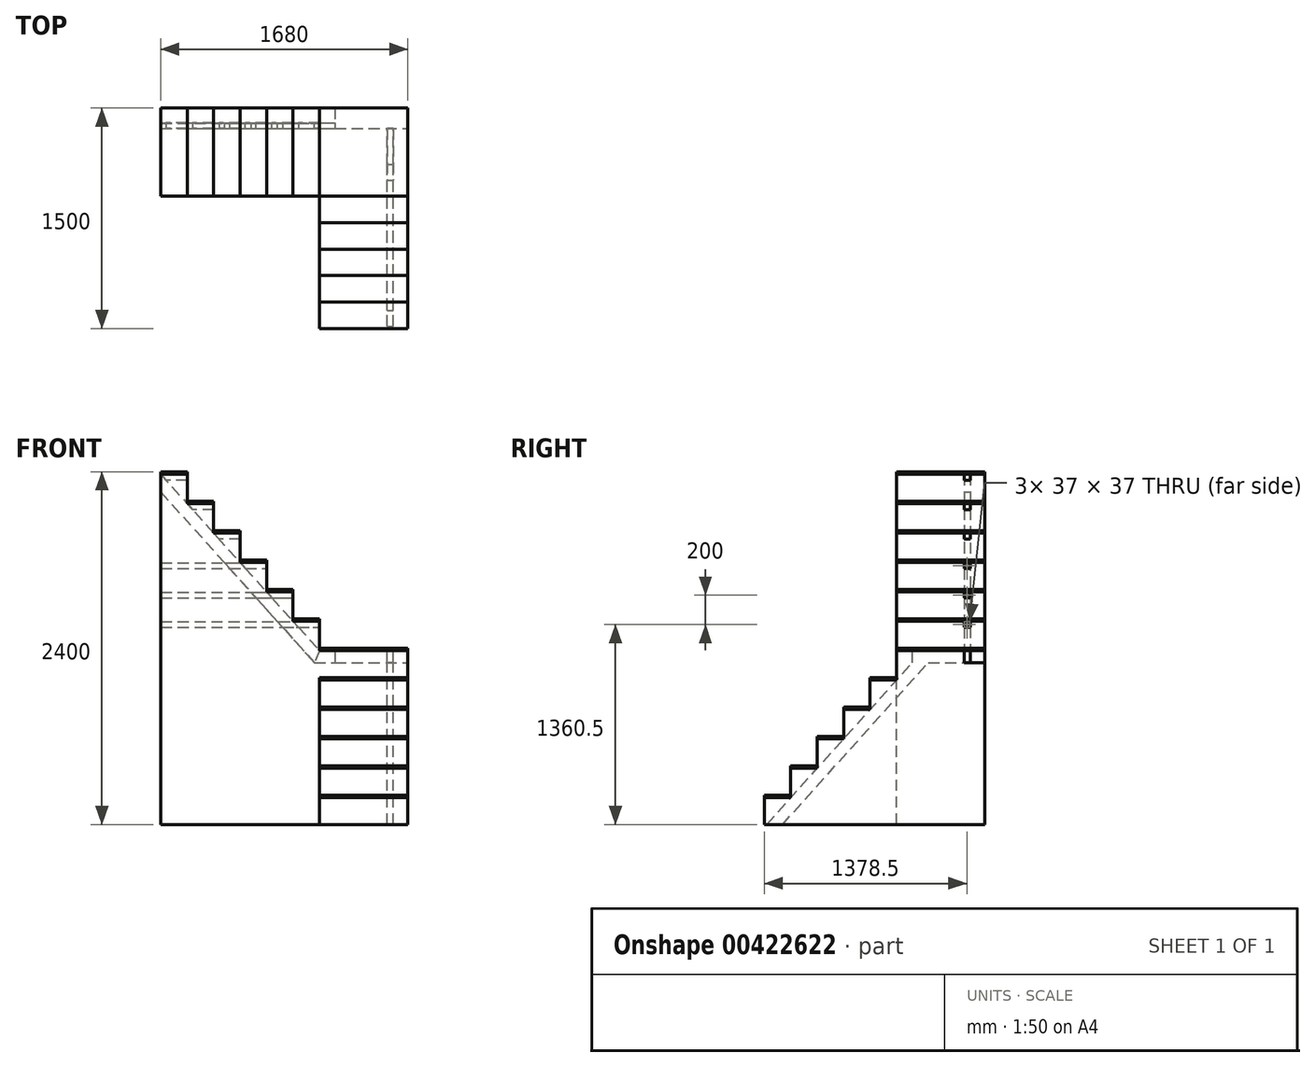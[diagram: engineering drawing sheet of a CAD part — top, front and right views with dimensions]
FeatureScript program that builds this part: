
annotation { "Feature Type Name" : "Feature", "Feature Type Description" : "" }
export const myFeature = defineFeature(function(context is Context, id is Id, definition is map)
    precondition{}
    {
        {
            var Q0;
            Q0=qCreatedBy(makeId("Front.planeOp"),FACE);
            var sketch = newSketch(context, id + "F0", { "sketchPlane" : qUnion([Q0])});
            skLineSegment(sketch, "E0.bottom", {"start": v(0, 0) * mm, "end": v(-600, 0) * mm});
            skLineSegment(sketch, "E0.top", {"start": v(0, 1200) * mm, "end": v(-600, 1200) * mm});
            skLineSegment(sketch, "E0.left", {"start": v(0, 0) * mm, "end": v(0, 1200) * mm});
            skLineSegment(sketch, "E0.right", {"start": v(-600, 0) * mm, "end": v(-600, 1200) * mm, "construction": true});
            skLineSegment(sketch, "E1", {"start": v(-600, 1200) * mm, "end": v(-600, 1400) * mm});
            skLineSegment(sketch, "E2", {"start": v(-600, 1400) * mm, "end": v(-780, 1400) * mm});
            skLineSegment(sketch, "E3", {"start": v(-780, 1400) * mm, "end": v(-780, 1600) * mm});
            skLineSegment(sketch, "E4", {"start": v(-780, 1600) * mm, "end": v(-960, 1600) * mm});
            skLineSegment(sketch, "E5", {"start": v(-960, 1600) * mm, "end": v(-960, 1800) * mm});
            skLineSegment(sketch, "E6", {"start": v(-960, 1800) * mm, "end": v(-1140, 1800) * mm});
            skLineSegment(sketch, "E7", {"start": v(-1140, 1800) * mm, "end": v(-1140, 2000) * mm});
            skLineSegment(sketch, "E8", {"start": v(-1140, 2000) * mm, "end": v(-1320, 2000) * mm});
            skLineSegment(sketch, "E9", {"start": v(-1320, 2000) * mm, "end": v(-1320, 2200) * mm});
            skLineSegment(sketch, "E10", {"start": v(-1320, 2200) * mm, "end": v(-1500, 2200) * mm});
            skLineSegment(sketch, "E11", {"start": v(-1500, 2200) * mm, "end": v(-1500, 2400) * mm});
            skLineSegment(sketch, "E12", {"start": v(-1500, 2400) * mm, "end": v(-1680, 2400) * mm});
            skLineSegment(sketch, "E13", {"start": v(-1680, 2400) * mm, "end": v(-1680, 0) * mm});
            skLineSegment(sketch, "E14", {"start": v(-1680, 0) * mm, "end": v(-600, 0) * mm});
            skLineSegment(sketch, "E15", {"start": v(-1680, 2400) * mm, "end": v(-1680, 2600) * mm, "construction": true});
            skLineSegment(sketch, "E16", {"start": v(-1680, 2600) * mm, "end": v(-2502.05, 2600) * mm, "construction": true});
            skLineSegment(sketch, "E17", {"start": v(-1680, 2582) * mm, "end": v(-2575.09, 2582) * mm, "construction": true});
            skLineSegment(sketch, "E18", {"start": v(-1680, 2382) * mm, "end": v(-1730, 2382) * mm, "construction": true});
            skLineSegment(sketch, "E19", {"start": v(-1730, 2382) * mm, "end": v(-1730, 2582) * mm, "construction": true});
            skSolve(sketch);
        }
        {
            var Q0;
            Q0=makeQuery(id+"F0.imprint","IMPRINT",FACE,{"disambiguationData":[TD([[makeQuery(id+"F0.imprint","IMPRINT",EDGE,{"derivedFrom":sQuery(id+"F0.wireOp",EDGE,"E0.bottom")}),-1.0]])]});
            extrude(context, id + "F1", {"entities" : qUnion([Q0]), "depth" : 600 * mm});
        }
        {
            var Q0;
            Q0=makeQuery(id+"F1.opExtrude","SWEPT_FACE",FACE,{"disambiguationData":[OSD([sQuery(id+"F0.wireOp",EDGE,"E0.left")])]});
            var sketch = newSketch(context, id + "F2", { "sketchPlane" : qUnion([Q0])});
            skLineSegment(sketch, "E20", {"start": v(-600, 0) * mm, "end": v(-1500, 0) * mm});
            skLineSegment(sketch, "E21", {"start": v(-1500, 0) * mm, "end": v(-1500, 200) * mm});
            skLineSegment(sketch, "E22", {"start": v(-1500, 200) * mm, "end": v(-1320, 200) * mm});
            skLineSegment(sketch, "E23", {"start": v(-1320, 200) * mm, "end": v(-1320, 400) * mm});
            skLineSegment(sketch, "E24", {"start": v(-1320, 400) * mm, "end": v(-1140, 400) * mm});
            skLineSegment(sketch, "E25", {"start": v(-1140, 400) * mm, "end": v(-1140, 600) * mm});
            skLineSegment(sketch, "E26", {"start": v(-1140, 600) * mm, "end": v(-960, 600) * mm});
            skLineSegment(sketch, "E27", {"start": v(-960, 600) * mm, "end": v(-960, 800) * mm});
            skLineSegment(sketch, "E28", {"start": v(-960, 800) * mm, "end": v(-780, 800) * mm});
            skLineSegment(sketch, "E29", {"start": v(-780, 800) * mm, "end": v(-780, 1000) * mm});
            skLineSegment(sketch, "E30", {"start": v(-780, 1000) * mm, "end": v(-600, 1000) * mm});
            skSolve(sketch);
        }
        {
            var Q0;
            Q0 = qSketchRegion(id + "F2", true);
            var Q1;
            {var subQ0=sQuery(id+"F2.wireOp",EDGE,"E20");Q1=makeQuery(id+"F2.imprint","IMPRINT",FACE,{"disambiguationData":[TD([[makeQuery(id+"F2.imprint","IMPRINT",EDGE,{"derivedFrom":subQ0}),-1.0]])]});}
            extrude(context, id + "F3", {"entities" : qUnion([Q0, Q1]), "operationType" : NewBodyOperationType.ADD, "oppositeDirection" : true, "depth" : 600 * mm});
        }
        {
            var Q0;
            Q0=makeQuery(id+"F1.opExtrude","SWEPT_FACE",FACE,{"disambiguationData":[OSD([sQuery(id+"F0.wireOp",EDGE,"E12")])]});
            var Q1;
            Q1=makeQuery(id+"F1.opExtrude","SWEPT_FACE",FACE,{"disambiguationData":[OSD([sQuery(id+"F0.wireOp",EDGE,"E10")])]});
            var Q2;
            Q2=makeQuery(id+"F1.opExtrude","SWEPT_FACE",FACE,{"disambiguationData":[OSD([sQuery(id+"F0.wireOp",EDGE,"E8")])]});
            var Q3;
            Q3=makeQuery(id+"F1.opExtrude","SWEPT_FACE",FACE,{"disambiguationData":[OSD([sQuery(id+"F0.wireOp",EDGE,"E6")])]});
            var Q4;
            Q4=makeQuery(id+"F1.opExtrude","SWEPT_FACE",FACE,{"disambiguationData":[OSD([sQuery(id+"F0.wireOp",EDGE,"E4")])]});
            var Q5;
            Q5=makeQuery(id+"F1.opExtrude","SWEPT_FACE",FACE,{"disambiguationData":[OSD([sQuery(id+"F0.wireOp",EDGE,"E2")])]});
            var Q6;
            Q6=makeQuery(id+"F1.opExtrude","SWEPT_FACE",FACE,{"disambiguationData":[OSD([sQuery(id+"F0.wireOp",EDGE,"E0.top")])]});
            var Q7;
            Q7=makeQuery(id+"F3.opExtrude","SWEPT_FACE",FACE,{"disambiguationData":[OSD([sQuery(id+"F2.wireOp",EDGE,"E30")])]});
            var Q8;
            Q8=makeQuery(id+"F3.opExtrude","SWEPT_FACE",FACE,{"disambiguationData":[OSD([sQuery(id+"F2.wireOp",EDGE,"E28")])]});
            var Q9;
            Q9=makeQuery(id+"F3.opExtrude","SWEPT_FACE",FACE,{"disambiguationData":[OSD([sQuery(id+"F2.wireOp",EDGE,"E26")])]});
            var Q10;
            Q10=makeQuery(id+"F3.opExtrude","SWEPT_FACE",FACE,{"disambiguationData":[OSD([sQuery(id+"F2.wireOp",EDGE,"E24")])]});
            var Q11;
            Q11=makeQuery(id+"F3.opExtrude","SWEPT_FACE",FACE,{"disambiguationData":[OSD([sQuery(id+"F2.wireOp",EDGE,"E22")])]});
            extrude(context, id + "F4", {"entities" : qUnion([Q0, Q1, Q2, Q3, Q4, Q5, Q6, Q7, Q8, Q9, Q10, Q11]), "oppositeDirection" : true, "depth" : 18 * mm});
        }
        {
            var Q0;
            Q0=qCreatedBy(makeId("Front.planeOp"),FACE);
            cPlane(context, id + "F5", {"entities" : qUnion([Q0]), "cplaneType" : CPlaneType.OFFSET, "offset" : 100 * mm, "width" : 150 * mm, "height" : 150 * mm});
        }
        {
            var Q0;
            Q0=qCreatedBy(id+"F5.planeOp",FACE);
            var sketch = newSketch(context, id + "F6", { "sketchPlane" : qUnion([Q0])});
            skLineSegment(sketch, "E31", {"start": v(-1680, 2382) * mm, "end": v(-600, 1182) * mm});
            skLineSegment(sketch, "E32", {"start": v(-1680, 2382) * mm, "end": v(-1680, 2262.41) * mm});
            skLineSegment(sketch, "E33", {"start": v(-1680, 2262.41) * mm, "end": v(-635.63, 1102) * mm});
            skLineSegment(sketch, "E34", {"start": v(-635.63, 1102) * mm, "end": v(-600, 1182) * mm});
            skLineSegment(sketch, "E35", {"start": v(-600, 1182) * mm, "end": v(-535.87, 1182) * mm, "construction": true});
            skSolve(sketch);
        }
        {
            var Q0;
            Q0 = qSketchRegion(id + "F6", true);
            extrude(context, id + "F7", {"entities" : qUnion([Q0]), "depth" : 40 * mm});
        }
        {
            var Q0;
            Q0=qCreatedBy(id+"F5.planeOp",FACE);
            var sketch = newSketch(context, id + "F8", { "sketchPlane" : qUnion([Q0])});
            skLineSegment(sketch, "E36.bottom", {"start": v(-600, 1182) * mm, "end": v(0, 1182) * mm});
            skLineSegment(sketch, "E36.top", {"start": v(-635.63, 1102) * mm, "end": v(0, 1102) * mm});
            skLineSegment(sketch, "E36.right", {"start": v(0, 1182) * mm, "end": v(0, 1102) * mm});
            skLineSegment(sketch, "E37", {"start": v(-600, 1182) * mm, "end": v(-635.63, 1102) * mm});
            skSolve(sketch);
        }
        {
            var Q0;
            Q0 = qSketchRegion(id + "F8", true);
            extrude(context, id + "F9", {"entities" : qUnion([Q0]), "depth" : 40 * mm});
        }
        {
            var Q0;
            Q0=makeQuery(id+"F7.opExtrude","CAP_FACE",FACE,{"disambiguationData":[OSD([sQuery(id+"F6.wireOp",EDGE,"E31"),sQuery(id+"F6.wireOp",EDGE,"E32"),sQuery(id+"F6.wireOp",EDGE,"E33"),sQuery(id+"F6.wireOp",EDGE,"E34")])],"isStart":false});
            var sketch = newSketch(context, id + "F10", { "sketchPlane" : qUnion([Q0])});
            skLineSegment(sketch, "E38", {"start": v(-1680, 2382) * mm, "end": v(-1500, 2382) * mm});
            skLineSegment(sketch, "E39", {"start": v(-1500, 2382) * mm, "end": v(-1500, 2342) * mm});
            skLineSegment(sketch, "E40", {"start": v(-1500, 2342) * mm, "end": v(-1644, 2342) * mm});
            skLineSegment(sketch, "E41", {"start": v(-1644, 2342) * mm, "end": v(-1680, 2382) * mm});
            skLineSegment(sketch, "E42.1.0.0", {"start": v(-1500, 2182) * mm, "end": v(-1320, 2182) * mm});
            skLineSegment(sketch, "E42.1.0.1", {"start": v(-1320, 2142) * mm, "end": v(-1464, 2142) * mm});
            skLineSegment(sketch, "E42.1.0.2", {"start": v(-1464, 2142) * mm, "end": v(-1500, 2182) * mm});
            skLineSegment(sketch, "E42.1.0.3", {"start": v(-1320, 2182) * mm, "end": v(-1320, 2142) * mm});
            skLineSegment(sketch, "E42.2.0.0", {"start": v(-1320, 1982) * mm, "end": v(-1140, 1982) * mm});
            skLineSegment(sketch, "E42.2.0.1", {"start": v(-1140, 1942) * mm, "end": v(-1284, 1942) * mm});
            skLineSegment(sketch, "E42.2.0.2", {"start": v(-1284, 1942) * mm, "end": v(-1320, 1982) * mm});
            skLineSegment(sketch, "E42.2.0.3", {"start": v(-1140, 1982) * mm, "end": v(-1140, 1942) * mm});
            skLineSegment(sketch, "E42.3.0.0", {"start": v(-1140, 1782) * mm, "end": v(-960, 1782) * mm});
            skLineSegment(sketch, "E42.3.0.1", {"start": v(-960, 1742) * mm, "end": v(-1104, 1742) * mm});
            skLineSegment(sketch, "E42.3.0.2", {"start": v(-1104, 1742) * mm, "end": v(-1140, 1782) * mm});
            skLineSegment(sketch, "E42.3.0.3", {"start": v(-960, 1782) * mm, "end": v(-960, 1742) * mm});
            skLineSegment(sketch, "E42.4.0.0", {"start": v(-960, 1582) * mm, "end": v(-780, 1582) * mm});
            skLineSegment(sketch, "E42.4.0.1", {"start": v(-780, 1542) * mm, "end": v(-924, 1542) * mm});
            skLineSegment(sketch, "E42.4.0.2", {"start": v(-924, 1542) * mm, "end": v(-960, 1582) * mm});
            skLineSegment(sketch, "E42.4.0.3", {"start": v(-780, 1582) * mm, "end": v(-780, 1542) * mm});
            skLineSegment(sketch, "E42.5.0.0", {"start": v(-780, 1382) * mm, "end": v(-600, 1382) * mm});
            skLineSegment(sketch, "E42.5.0.1", {"start": v(-600, 1342) * mm, "end": v(-744, 1342) * mm});
            skLineSegment(sketch, "E42.5.0.2", {"start": v(-744, 1342) * mm, "end": v(-780, 1382) * mm});
            skLineSegment(sketch, "E42.5.0.3", {"start": v(-600, 1382) * mm, "end": v(-600, 1342) * mm});
            skLineSegment(sketch, "E42.direction1", {"start": v(-1644, 2342) * mm, "end": v(-1464, 2142) * mm, "construction": true});
            skSolve(sketch);
        }
        {
            var Q0;
            Q0 = qSketchRegion(id + "F10", true);
            extrude(context, id + "F11", {"entities" : qUnion([Q0]), "oppositeDirection" : true, "depth" : 40 * mm});
        }
        {
            var Q0;
            Q0=makeQuery(id+"F11.opExtrude","SWEPT_FACE",FACE,{"disambiguationData":[OSD([sQuery(id+"F10.wireOp",EDGE,"E42.5.0.3")])]});
            var sketch = newSketch(context, id + "F12", { "sketchPlane" : qUnion([Q0])});
            skLineSegment(sketch, "E43.bottom", {"start": v(-140, 1342) * mm, "end": v(-103, 1342) * mm});
            skLineSegment(sketch, "E43.top", {"start": v(-140, 1379) * mm, "end": v(-103, 1379) * mm});
            skLineSegment(sketch, "E43.left", {"start": v(-140, 1342) * mm, "end": v(-140, 1379) * mm});
            skLineSegment(sketch, "E43.right", {"start": v(-103, 1342) * mm, "end": v(-103, 1379) * mm});
            skLineSegment(sketch, "E44.bottom", {"start": v(-140, 1542) * mm, "end": v(-103, 1542) * mm});
            skLineSegment(sketch, "E44.top", {"start": v(-140, 1579) * mm, "end": v(-103, 1579) * mm});
            skLineSegment(sketch, "E44.left", {"start": v(-140, 1542) * mm, "end": v(-140, 1579) * mm});
            skLineSegment(sketch, "E44.right", {"start": v(-103, 1542) * mm, "end": v(-103, 1579) * mm});
            skLineSegment(sketch, "E45.bottom", {"start": v(-140, 1742) * mm, "end": v(-103, 1742) * mm});
            skLineSegment(sketch, "E45.top", {"start": v(-140, 1779) * mm, "end": v(-103, 1779) * mm});
            skLineSegment(sketch, "E45.left", {"start": v(-140, 1742) * mm, "end": v(-140, 1779) * mm});
            skLineSegment(sketch, "E45.right", {"start": v(-103, 1742) * mm, "end": v(-103, 1779) * mm});
            skSolve(sketch);
        }
        {
            var Q0;
            Q0=makeQuery(id+"F12.imprint","IMPRINT",FACE,{"disambiguationData":[TD([[makeQuery(id+"F12.imprint","IMPRINT",EDGE,{"derivedFrom":sQuery(id+"F12.wireOp",EDGE,"E43.bottom")}),-1.0]])]});
            var Q1;
            Q1=makeQuery(id+"F12.imprint","IMPRINT",FACE,{"disambiguationData":[TD([[makeQuery(id+"F12.imprint","IMPRINT",EDGE,{"derivedFrom":sQuery(id+"F12.wireOp",EDGE,"E44.bottom")}),1.0]])]});
            var Q2;
            Q2=makeQuery(id+"F12.imprint","IMPRINT",FACE,{"disambiguationData":[TD([[makeQuery(id+"F12.imprint","IMPRINT",EDGE,{"derivedFrom":sQuery(id+"F12.wireOp",EDGE,"E45.bottom")}),1.0]])]});
            extrude(context, id + "F13", {"entities" : qUnion([Q0, Q1, Q2]), "operationType" : NewBodyOperationType.REMOVE, "endBound" : BoundingType.THROUGH_ALL, "oppositeDirection" : true, "depth" : 25 * mm});
        }
        {
            var Q0;
            Q0=qCreatedBy(makeId("Right.planeOp"),FACE);
            cPlane(context, id + "F14", {"entities" : qUnion([Q0]), "cplaneType" : CPlaneType.OFFSET, "offset" : 100 * mm, "oppositeDirection" : true, "width" : 150 * mm, "height" : 150 * mm});
        }
        {
            var Q0;
            Q0=qCreatedBy(id+"F14.planeOp",FACE);
            var sketch = newSketch(context, id + "F15", { "sketchPlane" : qUnion([Q0])});
            skLineSegment(sketch, "E46", {"start": v(-1483.8, 0) * mm, "end": v(-420, 1182) * mm});
            skLineSegment(sketch, "E47", {"start": v(-1483.8, 0) * mm, "end": v(-1376.17, 0) * mm});
            skLineSegment(sketch, "E48", {"start": v(-1376.17, 0) * mm, "end": v(-384.37, 1102) * mm});
            skLineSegment(sketch, "E49", {"start": v(-420, 1182) * mm, "end": v(-384.37, 1102) * mm});
            skLineSegment(sketch, "E50", {"start": v(-384.37, 1102) * mm, "end": v(-384.37, 1182) * mm, "construction": true});
            skLineSegment(sketch, "E51", {"start": v(-420, 1182) * mm, "end": v(0, 1182) * mm});
            skLineSegment(sketch, "E52", {"start": v(-384.37, 1102) * mm, "end": v(0, 1102) * mm});
            skLineSegment(sketch, "E53", {"start": v(0, 1102) * mm, "end": v(0, 1182) * mm});
            skLineSegment(sketch, "E54", {"start": v(-492, 1102) * mm, "end": v(-492, 1182) * mm});
            skLineSegment(sketch, "E55", {"start": v(-420, 1182) * mm, "end": v(-492, 1182) * mm});
            skSolve(sketch);
        }
        {
            var Q0;
            Q0 = qSketchRegion(id + "F15", true);
            extrude(context, id + "F16", {"entities" : qUnion([Q0]), "oppositeDirection" : true, "depth" : 40 * mm});
        }
        {
            var Q0;
            Q0=makeQuery(id+"F9.opExtrude","CAP_FACE",FACE,{"disambiguationData":[OSD([sQuery(id+"F8.wireOp",EDGE,"E36.bottom"),sQuery(id+"F8.wireOp",EDGE,"E36.top"),sQuery(id+"F8.wireOp",EDGE,"E36.right"),sQuery(id+"F8.wireOp",EDGE,"E37")])],"isStart":false});
            var sketch = newSketch(context, id + "F17", { "sketchPlane" : qUnion([Q0])});
            skLineSegment(sketch, "E56.bottom", {"start": v(-495.76, 1182) * mm, "end": v(0, 1182) * mm});
            skLineSegment(sketch, "E56.top", {"start": v(-495.76, 1102) * mm, "end": v(0, 1102) * mm});
            skLineSegment(sketch, "E56.left", {"start": v(-495.76, 1182) * mm, "end": v(-495.76, 1102) * mm});
            skLineSegment(sketch, "E56.right", {"start": v(0, 1182) * mm, "end": v(0, 1102) * mm});
            skSolve(sketch);
        }
        {
            var Q0;
            Q0 = qSketchRegion(id + "F17", true);
            extrude(context, id + "F18", {"entities" : qUnion([Q0]), "operationType" : NewBodyOperationType.REMOVE, "endBound" : BoundingType.THROUGH_ALL, "oppositeDirection" : true, "depth" : 25 * mm});
        }
    });
